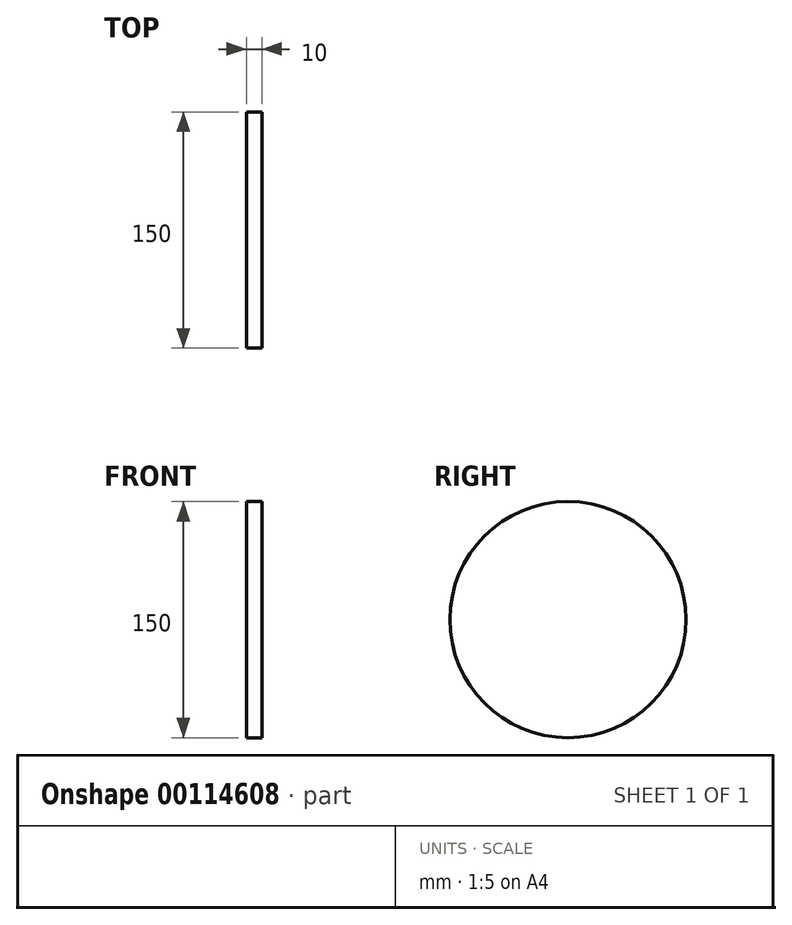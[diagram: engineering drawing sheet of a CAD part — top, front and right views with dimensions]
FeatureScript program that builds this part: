
annotation { "Feature Type Name" : "Feature", "Feature Type Description" : "" }
export const myFeature = defineFeature(function(context is Context, id is Id, definition is map)
    precondition{}
    {
        {
            var Q0;
            Q0=qCreatedBy(makeId("Right.planeOp"),FACE);
            var sketch = newSketch(context, id + "F0", { "sketchPlane" : qUnion([Q0])});
            skCircle(sketch, "E0", {"center": v(0, 0) * mm, "radius": 75 * mm});
            skSolve(sketch);
        }
        {
            var Q0;
            Q0=makeQuery(id+"F0.imprint","IMPRINT",FACE,{"disambiguationData":[TD([[makeQuery(id+"F0.imprint","IMPRINT",EDGE,{"derivedFrom":sQuery(id+"F0.wireOp",EDGE,"E0")}),1.0]])]});
            extrude(context, id + "F2", {"entities" : qUnion([Q0]), "endBound" : BoundingType.SYMMETRIC, "depth" : 10 * mm});
        }
    });
